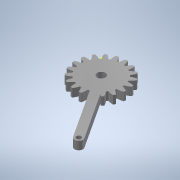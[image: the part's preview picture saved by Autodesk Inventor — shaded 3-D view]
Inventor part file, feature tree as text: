
AUTODESK INVENTOR PART (.ipt)
format: ipt  version: 2022 (Build 260153000, 153)  size: 325,632 bytes
history: native  units: mm (DEFAULTED — no unit token found)
features: sketch x9, extrude x7, plane x3, other x3, fillet x1
ambient origin geometry x8: Origin, YZ Plane, XZ Plane, XY Plane, X Axis, Y Axis, Z Axis, Center Point
bodies: Solid1 (feature_tree)
feature tree (23):
  extrude  "Extrusion1"  Depth=14.0mm TaperAngle=0.0deg
  plane  "Work Plane2"
  plane  "Work Plane8"
  plane  "Work Plane9"
  other  "Spur Gear"
  extrude  "Extrusion2"  Depth=10.0mm TaperAngle=0.0deg
  sketch  "Sketch4"  dims[d39=0.0mm d41=0.0mm]
  extrude  "Extrusion3"  Depth=1.65347mm TaperAngle=0.0deg
  extrude  "Extrusion4"  TaperAngle=0.0deg  [1 undecoded]
  extrude  "Extrusion5"  Depth=63.0mm
  extrude  "Extrusion6"  Depth=8.0mm
  fillet  "Fillet1"  Radius=3.0mm
  extrude  "Extrusion7"  Depth=10.0mm TaperAngle=0.0deg
  sketch  "Sketch1"  dims[d0=31.5mm d1=14.0mm d2=0.0mm]
  sketch  "Sketch2"  dims[d3=28.5mm d4=10.0mm d5=0.0mm]
  other  "Srf1"
  sketch  "Sketch3"  dims[d16=63.0mm d17=0.0mm d34=1.65347mm]
  sketch  "Sketch5"  dims[d43=63.0mm d46=63.0mm]
  sketch  "Sketch6"  dims[d47=0.0mm d48=0.0mm d49=8.0mm d50=3.0mm]
  sketch  "Sketch7"  dims[d51=1.4mm d52=10.0mm d53=0.0mm]
  sketch  "Sketch8"  dims[d54=14.0mm d55=0.0mm]
  sketch  "Sketch9"  dims[d57=47.0mm d58=0.0mm d60=5.0mm d61=5.0mm d62=0.0mm d66=5.0mm d67=0.0mm d68=2.5mm d69=3.0mm d70=5.0mm d71=0.0mm]
  other  "Pitch Diameter"
note: 1 required parameter value undecoded (feature->parameter linkage not recoverable at this tier; creation-order binding heuristic only, values carry confidence <= 0.55)
